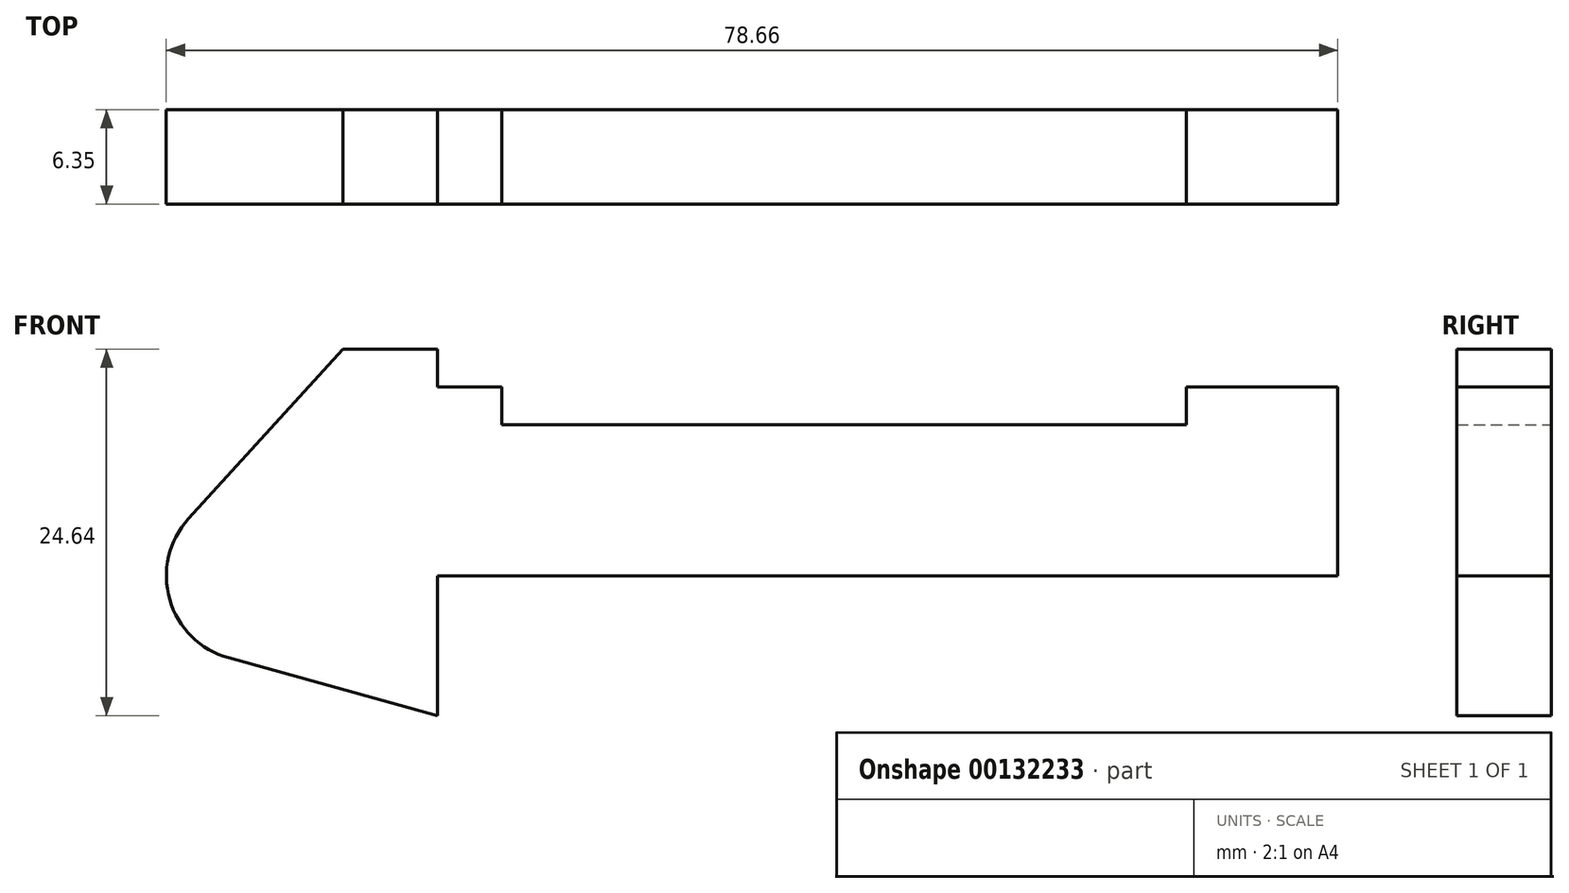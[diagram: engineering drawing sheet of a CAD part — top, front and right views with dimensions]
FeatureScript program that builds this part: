
annotation { "Feature Type Name" : "Feature", "Feature Type Description" : "" }
export const myFeature = defineFeature(function(context is Context, id is Id, definition is map)
    precondition{}
    {
        {
            var Q0;
            Q0=qCreatedBy(makeId("Front.planeOp"),FACE);
            var sketch = newSketch(context, id + "F0", { "sketchPlane" : qUnion([Q0])});
            skLineSegment(sketch, "E0", {"start": v(0, 0) * mm, "end": v(0, 12.7) * mm});
            skLineSegment(sketch, "E1", {"start": v(0, 12.7) * mm, "end": v(10.16, 12.7) * mm});
            skLineSegment(sketch, "E2", {"start": v(10.16, 12.7) * mm, "end": v(10.16, 10.16) * mm});
            skLineSegment(sketch, "E3", {"start": v(10.16, 10.16) * mm, "end": v(56.13, 10.16) * mm});
            skLineSegment(sketch, "E4", {"start": v(56.13, 10.16) * mm, "end": v(56.13, 12.7) * mm});
            skLineSegment(sketch, "E5", {"start": v(56.13, 12.7) * mm, "end": v(66.3, 12.7) * mm});
            skLineSegment(sketch, "E6", {"start": v(66.3, 12.7) * mm, "end": v(66.3, 0) * mm});
            skLineSegment(sketch, "E7", {"start": v(66.3, 0) * mm, "end": v(0, 0) * mm});
            skLineSegment(sketch, "E8", {"start": v(5.84, 15.24) * mm, "end": v(-0.5, 15.24) * mm});
            skLineSegment(sketch, "E9", {"start": v(-0.5, 15.24) * mm, "end": v(-10.88, 3.85) * mm});
            skLineSegment(sketch, "E10", {"start": v(0, 0) * mm, "end": v(-6.65, 0) * mm});
            skCircle(sketch, "E11", {"center": v(-6.65, 0) * mm, "radius": 5.72 * mm});
            skCircle(sketch, "E12", {"center": v(-6.65, 0) * mm, "radius": 3.18 * mm});
            skLineSegment(sketch, "E13", {"start": v(5.84, 15.24) * mm, "end": v(5.84, -9.4) * mm});
            skLineSegment(sketch, "E14", {"start": v(5.84, -9.4) * mm, "end": v(-8.18, -5.5) * mm});
            skSolve(sketch);
        }
        {
            var Q0;
            {var subQ0=sQuery(id+"F0.wireOp",EDGE,"E14");Q0=makeQuery(id+"F0.imprint","IMPRINT",FACE,{"disambiguationData":[TD([[makeQuery(id+"F0.imprint","IMPRINT",EDGE,{"derivedFrom":subQ0}),-1.0]])]});}
            var Q1;
            {var subQ3=sQuery(id+"F0.wireOp",EDGE,"E0");Q1=makeQuery(id+"F0.imprint","IMPRINT",FACE,{"disambiguationData":[TD([[makeQuery(id+"F0.imprint","IMPRINT",EDGE,{"derivedFrom":subQ3}),1.0]])]});}
            var Q2;
            {var subQ4=sQuery(id+"F0.wireOp",EDGE,"E12");Q2=makeQuery(id+"F0.imprint","IMPRINT",FACE,{"disambiguationData":[TD([[makeQuery(id+"F0.imprint","IMPRINT",EDGE,{"derivedFrom":subQ4}),-1.0]])]});}
            var Q3;
            {var subQ0=sQuery(id+"F0.wireOp",EDGE,"E2");Q3=makeQuery(id+"F0.imprint","IMPRINT",FACE,{"disambiguationData":[TD([[makeQuery(id+"F0.imprint","IMPRINT",EDGE,{"derivedFrom":subQ0}),-1.0]])]});}
            var Q4;
            {var subQ0=sQuery(id+"F0.wireOp",EDGE,"E0");Q4=makeQuery(id+"F0.imprint","IMPRINT",FACE,{"disambiguationData":[TD([[makeQuery(id+"F0.imprint","IMPRINT",EDGE,{"derivedFrom":subQ0}),-1.0]])]});}
            var Q5;
            {var subQ0=sQuery(id+"F0.wireOp",EDGE,"E12");Q5=makeQuery(id+"F0.imprint","IMPRINT",FACE,{"disambiguationData":[TD([[makeQuery(id+"F0.imprint","IMPRINT",EDGE,{"derivedFrom":subQ0}),1.0]])]});}
            extrude(context, id + "F1", {"entities" : qUnion([Q0, Q1, Q2, Q3, Q4, Q5]), "depth" : 6.35 * mm});
        }
        {
            var Q0;
            {var subQ0=sQuery(id+"F0.wireOp",EDGE,"E12");Q0=makeQuery(id+"F0.imprint","IMPRINT",FACE,{"disambiguationData":[TD([[makeQuery(id+"F0.imprint","IMPRINT",EDGE,{"derivedFrom":subQ0}),1.0]])]});}
            var Q1;
            {var subQ4=sQuery(id+"F0.wireOp",EDGE,"E12");Q1=makeQuery(id+"F0.imprint","IMPRINT",FACE,{"disambiguationData":[TD([[makeQuery(id+"F0.imprint","IMPRINT",EDGE,{"derivedFrom":subQ4}),-1.0]])]});}
            extrude(context, id + "F2", {"entities" : qUnion([Q0, Q1]), "operationType" : NewBodyOperationType.ADD, "depth" : 3.05 * mm});
        }
    });
